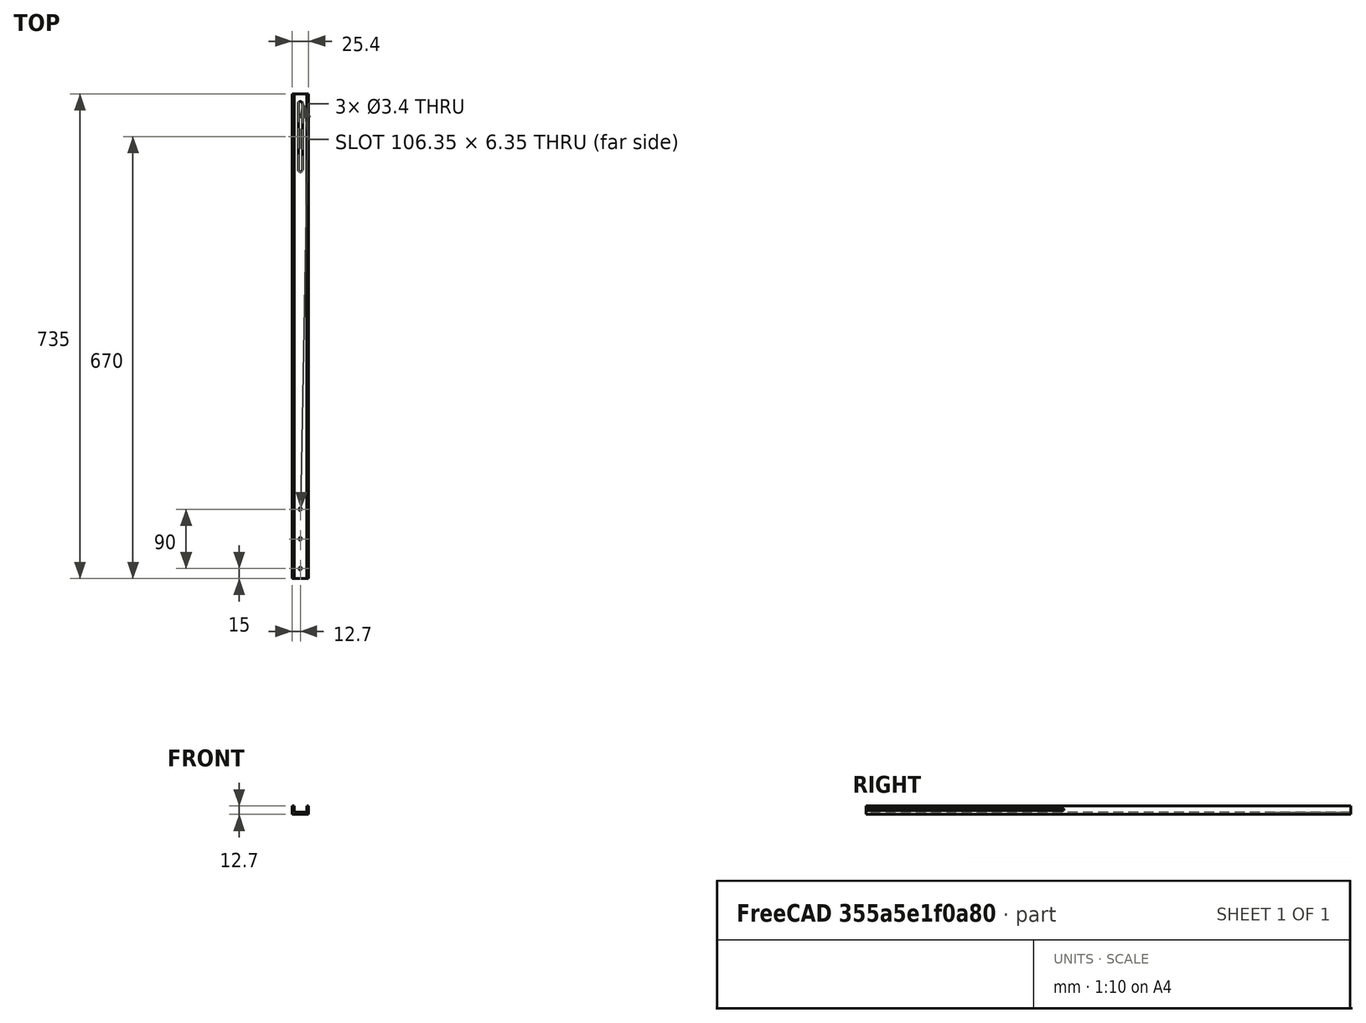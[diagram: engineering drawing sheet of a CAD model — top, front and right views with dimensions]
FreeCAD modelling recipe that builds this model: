
FCSTD DOCUMENT  (FreeCAD 0.20R29603 (Git))
Label: Channel
License: All rights reserved
LicenseURL: https://en.wikipedia.org/wiki/All_rights_reserved
objects: TechDraw::DrawViewDimension×7, Sketcher::SketchObject×3, TechDraw::DrawViewPart×3, PartDesign::Pocket×2, PartDesign::Pad×1, PartDesign::Hole×1, PartDesign::Point×1, PartDesign::Body×1, TechDraw::DrawSVGTemplate×1, TechDraw::DrawPage×1
note: 13 computed .brp shape members not serialized (recipe doc carries the construction recipe); baked Part::Feature solids carry a one-line shape summary decoded from their .brp

FEATURE [Sketcher::SketchObject] Sketch
  FullyConstrained = true
  MapMode = 5
  Placement = pos=(0,0,0) rot=(1,0,0;1.5708rad)
  Support = -> [XZ_Plane]
  sketch-geometry (9):
    g0: LineSegment StartX=-12.7 StartY=12.7 StartZ=0 EndX=-12.7 EndY=0 EndZ=0
    g1: LineSegment StartX=-12.7 StartY=0 StartZ=0 EndX=12.7 EndY=0 EndZ=0
    g2: LineSegment StartX=12.7 StartY=0 StartZ=0 EndX=12.7 EndY=12.7 EndZ=0
    g3: LineSegment StartX=12.7 StartY=12.7 StartZ=0 EndX=9.525 EndY=12.7 EndZ=0
    g4: LineSegment StartX=9.525 StartY=12.7 StartZ=0 EndX=9.525 EndY=3.175 EndZ=0
    g5: LineSegment StartX=9.525 StartY=3.175 StartZ=0 EndX=-9.525 EndY=3.175 EndZ=0
    g6: LineSegment StartX=-9.525 StartY=3.175 StartZ=0 EndX=-9.525 EndY=12.7 EndZ=0
    g7: LineSegment StartX=-9.525 StartY=12.7 StartZ=0 EndX=-12.7 EndY=12.7 EndZ=0
    g8: LineSegment StartX=-9.525 StartY=3.175 StartZ=0 EndX=-9.525 EndY=0 EndZ=0
  constraints (26):
    c: Coincident(g0,g1)
    c: Horizontal(g1)
    c: Coincident(g1,g2)
    c: Vertical(g2)
    c: Coincident(g2,g3)
    c: Coincident(g3,g4)
    c: Coincident(g4,g5)
    c: Coincident(g5,g6)
    c: Coincident(g6,g7)
    c: Coincident(g7,g0)
    c: Vertical(g0)
    c: Vertical(g6)
    c: Vertical(g4)
    c: Horizontal(g3)
    c: Horizontal(g7)
    c: Equal(g7,g3)
    c: Equal(g6,g4)
    c: Coincident(g8,g5)
    c: PointOnObject(g8,g1)
    c: Vertical(g8)
    c: Equal(g7,g8)
    c: DistanceX(g3,g3) = 3.175
    c: DistanceX(g1,g1) = 25.4
    c: DistanceY(g2,g2) = 12.7  'height'
    c: Symmetric(g4,g5,g-2)
    c: PointOnObject(g-1,g1)
FEATURE [PartDesign::Pad] Pad
  AlongSketchNormal = false
  Direction = (0,-1,-2e-16)
  Length = 735
  Length2 = 10
  Midplane = true
  Profile = -> Sketch
  ReferenceAxis = -> Sketch [N_Axis]
  Type = 0
FEATURE [Sketcher::SketchObject] Sketch001
  FullyConstrained = false
  MapMode = 5
  Placement = pos=(0,-367.5,0) rot=(1,0,0;1.5708rad)
  Support = -> [Pad]
  expr: Constraints[20] = Sketch.Constraints.height - 5mm
  sketch-geometry (9):
    g0: LineSegment StartX=-33.5342 StartY=9.2875 StartZ=0 EndX=-11.1125 EndY=9.2875 EndZ=0
    g1: LineSegment StartX=-11.1125 StartY=9.2875 StartZ=0 EndX=-11.1125 EndY=6.1125 EndZ=0
    g2: LineSegment StartX=-11.1125 StartY=6.1125 StartZ=0 EndX=-33.5342 EndY=6.1125 EndZ=0
    g3: LineSegment StartX=-33.5342 StartY=6.1125 StartZ=0 EndX=-33.5342 EndY=9.2875 EndZ=0
    g4: LineSegment StartX=33.5342 StartY=6.1125 StartZ=0 EndX=11.1125 EndY=6.1125 EndZ=0
    g5: LineSegment StartX=11.1125 StartY=6.1125 StartZ=0 EndX=11.1125 EndY=9.2875 EndZ=0
    g6: LineSegment StartX=11.1125 StartY=9.2875 StartZ=0 EndX=33.5342 EndY=9.2875 EndZ=0
    g7: LineSegment StartX=33.5342 StartY=9.2875 StartZ=0 EndX=33.5342 EndY=6.1125 EndZ=0
    g8: GeomPoint X=1e-16 Y=7.7 Z=0
  constraints (23):
    c: Coincident(g0,g1)
    c: Coincident(g1,g2)
    c: Coincident(g2,g3)
    c: Coincident(g3,g0)
    c: Horizontal(g0)
    c: Horizontal(g2)
    c: Vertical(g1)
    c: Vertical(g3)
    c: Coincident(g4,g5)
    c: Coincident(g5,g6)
    c: Coincident(g6,g7)
    c: Coincident(g7,g4)
    c: Horizontal(g4)
    c: Horizontal(g6)
    c: Vertical(g7)
    c: PointOnObject(g8,g-2)
    c: Symmetric(g1,g5,g8)
    c: Symmetric(g4,g0,g8)
    c: Horizontal(g4,g1)
    c: Equal(g0,g6)
    c: DistanceY(g-1,g8) = 7.7
    c: DistanceY(g5,g5) = 3.175
    c: DistanceX(g-1,g4) = 11.1125
FEATURE [PartDesign::Pocket] Pocket
  AlongSketchNormal = false
  BaseFeature = -> Pad
  Direction = (0,1,-2e-16)
  Length = 300
  Length2 = 10
  Profile = -> Sketch001
  ReferenceAxis = -> Sketch001 [N_Axis]
  Type = 0
FEATURE [Sketcher::SketchObject] Sketch002
  ExternalGeometry = -> [Pocket]
  FullyConstrained = true
  MapMode = 5
  Placement = pos=(0,0,7e-16) rot=(1,0,0;3.14159rad)
  Support = -> [Pocket]
  sketch-geometry (9):
    g0: Circle CenterX=0 CenterY=352.5 CenterZ=0 NormalX=0 NormalY=0 NormalZ=1 AngleXU=0 Radius=1.6
    g1: Circle CenterX=0 CenterY=262.5 CenterZ=0 NormalX=0 NormalY=0 NormalZ=1 AngleXU=0 Radius=1.6
    g2: ArcOfCircle CenterX=0 CenterY=-252.5 CenterZ=0 NormalX=0 NormalY=0 NormalZ=1 AngleXU=0 Radius=3.175 StartAngle=-2.7e-15 EndAngle=3.14159
    g3: ArcOfCircle CenterX=0 CenterY=-352.5 CenterZ=0 NormalX=0 NormalY=0 NormalZ=1 AngleXU=0 Radius=3.175 StartAngle=3.14159 EndAngle=6.28319
    g4: LineSegment StartX=-3.175 StartY=-252.5 StartZ=0 EndX=-3.175 EndY=-352.5 EndZ=0
    g5: LineSegment StartX=3.175 StartY=-352.5 StartZ=0 EndX=3.175 EndY=-252.5 EndZ=0
    g6: GeomPoint X=0 Y=307.5 Z=0
    g7: GeomPoint X=0 Y=-302.5 Z=0
    g8: Circle CenterX=0 CenterY=307.5 CenterZ=0 NormalX=0 NormalY=0 NormalZ=1 AngleXU=0 Radius=1.6
  constraints (20):
    c: PointOnObject(g1,g-2)
    c: PointOnObject(g0,g-2)
    c: Equal(g1,g0)
    c: Tangent(g2,g4) = -1.5708
    c: Tangent(g4,g3) = -1.5708
    c: Tangent(g3,g5) = -1.5708
    c: Tangent(g5,g2) = -1.5708
    c: PointOnObject(g2,g-2)
    c: PointOnObject(g3,g-2)
    c: DistanceY(g1,g0) = 90
    c: DistanceY(g3,g2) = 100
    c: Radius(g2) = 3.175
    c: Symmetric(g0,g1,g6)
    c: Symmetric(g2,g3,g7)
    c: DistanceY(g7,g6) = 610
    c: Vertical(g4)
    c: Diameter(g0) = 3.2
    c: Coincident(g8,g6)
    c: Equal(g1,g8)
    c: DistanceY(g0,g-3) = 15
FEATURE [PartDesign::Pocket] Pocket001
  AlongSketchNormal = false
  BaseFeature = -> Pocket
  Direction = (0,-2e-16,1)
  Length = 0
  Length2 = 10
  Profile = -> Sketch002 [Edge6,Edge5,Edge4,Edge3]
  ReferenceAxis = -> Sketch002 [N_Axis]
  Type = 3
  UpToFace = -> Pocket [Face12]
FEATURE [PartDesign::Hole] Hole
  BaseFeature = -> Pocket001
  CustomThreadClearance = 0
  Depth = 1485.81
  DepthType = 1
  Diameter = 3.4
  DrillForDepth = false
  DrillPoint = 1
  DrillPointAngle = 118
  HoleCutCountersinkAngle = 90
  HoleCutCustomValues = false
  HoleCutDepth = 0
  HoleCutDiameter = 6.1
  HoleCutType = 2
  ModelThread = false
  Profile = -> Sketch002 [Edge2,Edge1,Edge7]
  Tapered = false
  TaperedAngle = 90
  ThreadClass = 0
  ThreadDepth = 1485.81
  ThreadDepthType = 0
  ThreadDirection = 0
  ThreadFit = 0
  ThreadSize = 9
  ThreadType = 1
  Threaded = false
  UseCustomThreadClearance = false
FEATURE [PartDesign::Point] DatumPoint
  AttacherType = Attacher::AttachEnginePoint
  AttachmentOffset = pos=(0,-200,0) rot=(0,0,1;0rad)
  MapMode = 37
  Placement = pos=(0,-209.752,-1.4e-15) rot=(0,0,1;0rad)
  Support = -> [Hole]
FEATURE [PartDesign::Body] Body  label="Channel"
  Group = -> [Sketch,Sketch001,Sketch002,Pad,Pocket,Pocket001,Hole,DatumPoint]
  Origin = -> Origin
  Tip = -> Hole
FEATURE [TechDraw::DrawSVGTemplate] Template
  Height = 297
  Orientation = 1
  Width = 420
FEATURE [TechDraw::DrawViewPart] View001  label="Top"
  CoarseView = false
  Direction = (0,0,1)
  Focus = 100
  HardHidden = false
  IsoCount = 0
  IsoHidden = false
  IsoVisible = false
  LockPosition = false
  Perspective = false
  Rotation = 0
  Scale = 0.5
  ScaleType = 0
  SeamHidden = false
  SeamVisible = true
  SmoothHidden = false
  SmoothVisible = true
  Source = -> [Hole]
  X = 209.57
  XDirection = (0,-1,0)
  Y = 244.118
FEATURE [TechDraw::DrawViewDimension] Dimension001
  AngleOverride = false
  Arbitrary = false
  ArbitraryTolerances = false
  EqualTolerance = true
  ExtensionAngle = 0
  FormatSpec = %.2w
  FormatSpecOverTolerance = %+.2w
  FormatSpecUnderTolerance = %+.2w
  Inverted = false
  LineAngle = 0
  LockPosition = false
  MeasureType = 1
  OverTolerance = 0
  References2D = -> [View001]
  Rotation = 0
  Scale = 0.5
  ScaleType = 0
  TheoreticalExact = false
  Type = 1
  UnderTolerance = 0
  X = -164.371
  Y = -33.0505
FEATURE [TechDraw::DrawViewDimension] Dimension
  AngleOverride = false
  Arbitrary = false
  ArbitraryTolerances = false
  EqualTolerance = true
  ExtensionAngle = 0
  FormatSpec = %.2w
  FormatSpecOverTolerance = %+.2w
  FormatSpecUnderTolerance = %+.2w
  Inverted = false
  LineAngle = 0
  LockPosition = false
  MeasureType = 1
  OverTolerance = 0
  References2D = -> [View001]
  Rotation = 0
  Scale = 0.5
  ScaleType = 0
  TheoreticalExact = false
  Type = 1
  UnderTolerance = 0
  X = 0.406176
  Y = -32.9406
FEATURE [TechDraw::DrawViewPart] View002  label="Bottom"
  CoarseView = false
  Direction = (0,0,-1)
  Focus = 100
  HardHidden = false
  IsoCount = 0
  IsoHidden = false
  IsoVisible = false
  LockPosition = false
  Perspective = false
  Rotation = 0
  Scale = 0.5
  ScaleType = 0
  SeamHidden = false
  SeamVisible = true
  SmoothHidden = false
  SmoothVisible = true
  Source = -> [Hole]
  X = 209.719
  XDirection = (0,-1,0)
  Y = 176.627
FEATURE [TechDraw::DrawViewDimension] Dimension004
  AngleOverride = false
  Arbitrary = false
  ArbitraryTolerances = false
  EqualTolerance = true
  ExtensionAngle = 0
  FormatSpec = 3X ⌀%.2w THRU ⌵6.1x90°
  FormatSpecOverTolerance = %+.2w
  FormatSpecUnderTolerance = %+.2w
  Inverted = false
  LineAngle = 0
  LockPosition = false
  MeasureType = 1
  OverTolerance = 0
  References2D = -> [View002]
  Rotation = 0
  Scale = 0.5
  ScaleType = 0
  TheoreticalExact = false
  Type = 5
  UnderTolerance = 0
  X = 73.7573
  Y = -30.0116
FEATURE [TechDraw::DrawViewDimension] Dimension005
  AngleOverride = false
  Arbitrary = false
  ArbitraryTolerances = false
  EqualTolerance = true
  ExtensionAngle = 0
  FormatSpec = %.2w (1/4")
  FormatSpecOverTolerance = %+.2w
  FormatSpecUnderTolerance = %+.2w
  Inverted = false
  LineAngle = 0
  LockPosition = false
  MeasureType = 1
  OverTolerance = 0
  References2D = -> [View002]
  Rotation = 0
  Scale = 0.5
  ScaleType = 0
  TheoreticalExact = false
  Type = 2
  UnderTolerance = 0
  X = -99.1893
  Y = -39.547
FEATURE [TechDraw::DrawViewDimension] Dimension006
  AngleOverride = false
  Arbitrary = false
  ArbitraryTolerances = false
  EqualTolerance = true
  ExtensionAngle = 0
  FormatSpec = %.2w
  FormatSpecOverTolerance = %+.2w
  FormatSpecUnderTolerance = %+.2w
  Inverted = false
  LineAngle = 0
  LockPosition = false
  MeasureType = 1
  OverTolerance = 0
  References2D = -> [View001]
  Rotation = 0
  Scale = 0.5
  ScaleType = 0
  TheoreticalExact = false
  Type = 1
  UnderTolerance = 0
  X = 164.448
  Y = -33.1003
FEATURE [TechDraw::DrawViewPart] View  label="Front"
  Caption = 1:1
  CoarseView = false
  Direction = (0,-1,0)
  Focus = 100
  HardHidden = false
  IsoCount = 0
  IsoHidden = false
  IsoVisible = false
  LockPosition = false
  Perspective = false
  Rotation = 0
  ScaleType = 2
  SeamHidden = false
  SeamVisible = true
  SmoothHidden = false
  SmoothVisible = true
  Source = -> [Hole]
  X = 211.419
  XDirection = (1,0,0)
  Y = 112.899
FEATURE [TechDraw::DrawViewDimension] Dimension008
  AngleOverride = false
  Arbitrary = false
  ArbitraryTolerances = false
  EqualTolerance = true
  ExtensionAngle = 0
  FormatSpec = %.2w (1/16")
  FormatSpecOverTolerance = %+.2w
  FormatSpecUnderTolerance = %+.2w
  Inverted = false
  LineAngle = 0
  LockPosition = false
  MeasureType = 1
  OverTolerance = 0
  References2D = -> [View]
  Rotation = 0
  Scale = 0.5
  ScaleType = 0
  TheoreticalExact = false
  Type = 1
  UnderTolerance = 0
  X = -63.1056
  Y = -24.338
FEATURE [TechDraw::DrawViewDimension] Dimension007
  AngleOverride = false
  Arbitrary = false
  ArbitraryTolerances = false
  EqualTolerance = true
  ExtensionAngle = 0
  FormatSpec = %.2w (1/8")
  FormatSpecOverTolerance = %+.2w
  FormatSpecUnderTolerance = %+.2w
  Inverted = false
  LineAngle = 0
  LockPosition = false
  MeasureType = 1
  OverTolerance = 0
  References2D = -> [View]
  Rotation = 0
  Scale = 0.5
  ScaleType = 0
  TheoreticalExact = false
  Type = 2
  UnderTolerance = 0
  X = -36.0526
  Y = 20.6653
FEATURE [TechDraw::DrawPage] Page
  KeepUpdated = true
  NextBalloonIndex = 1
  ProjectionType = 0
  Scale = 0.5
  Template = -> Template
  Views = -> [View001,View,Dimension001,Dimension,View002,Dimension004,Dimension005,Dimension006,Dimension007,Dimension008]
